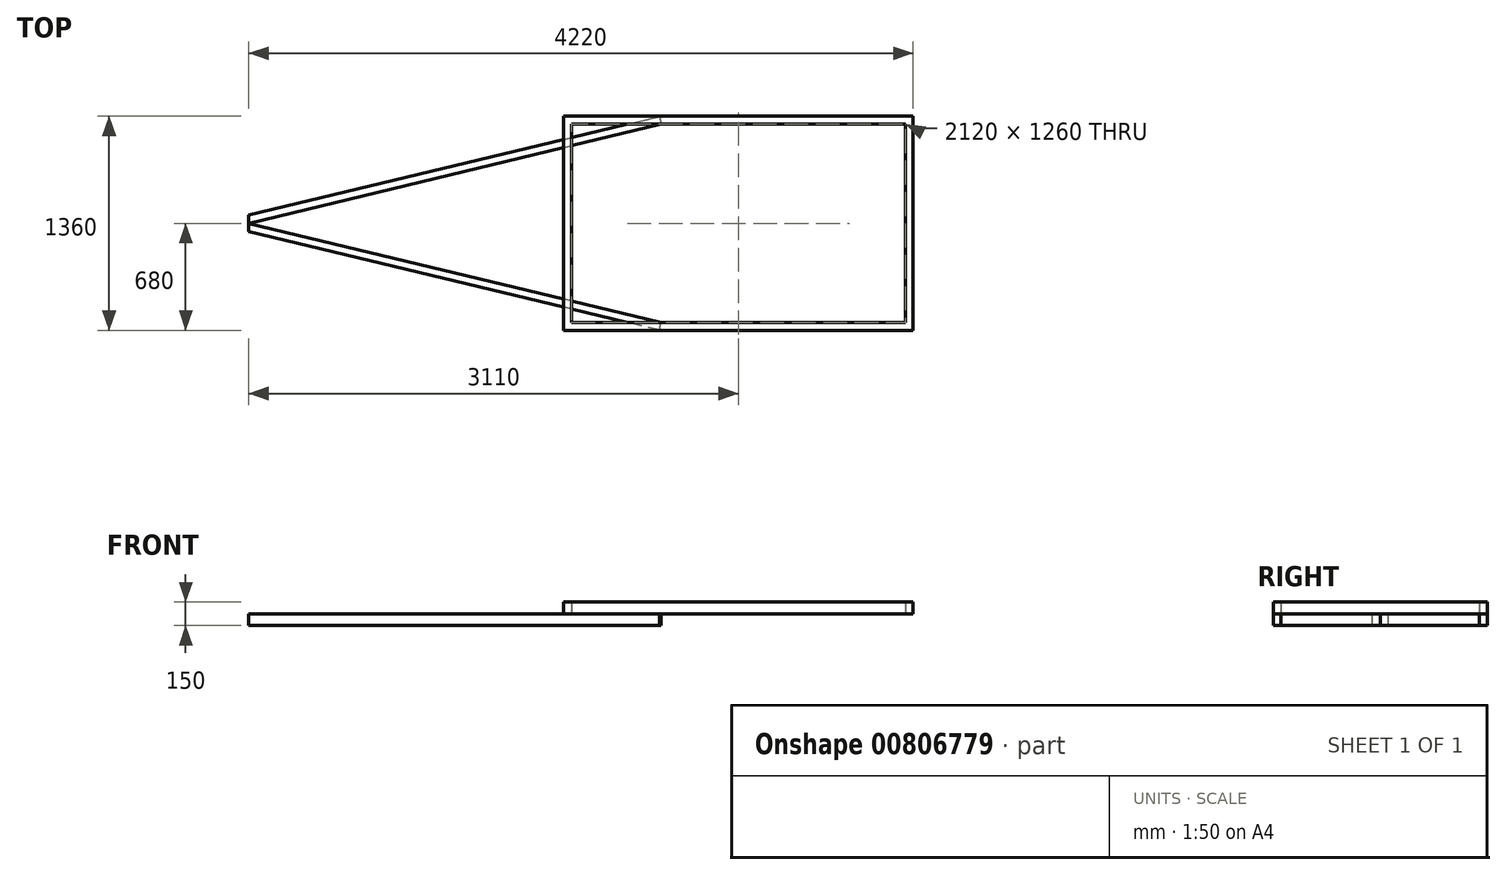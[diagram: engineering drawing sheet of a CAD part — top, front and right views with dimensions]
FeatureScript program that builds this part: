
annotation { "Feature Type Name" : "Feature", "Feature Type Description" : "" }
export const myFeature = defineFeature(function(context is Context, id is Id, definition is map)
    precondition{}
    {
        {
            var Q0;
            Q0=qCreatedBy(makeId("Top.planeOp"),FACE);
            var sketch = newSketch(context, id + "F0", { "sketchPlane" : qUnion([Q0])});
            skLineSegment(sketch, "E0.bottom", {"start": v(1110, 680) * mm, "end": v(-1110, 680) * mm});
            skLineSegment(sketch, "E0.top", {"start": v(1110, -680) * mm, "end": v(-1110, -680) * mm});
            skLineSegment(sketch, "E0.left", {"start": v(1110, 680) * mm, "end": v(1110, -680) * mm});
            skLineSegment(sketch, "E0.right", {"start": v(-1110, 680) * mm, "end": v(-1110, -680) * mm});
            skPoint(sketch, "E0.middle", {"position": v(0, 0) * mm});
            skLineSegment(sketch, "E1.0", {"start": v(1060, 630) * mm, "end": v(-1060, 630) * mm});
            skLineSegment(sketch, "E1.1", {"start": v(1060, 630) * mm, "end": v(1060, -630) * mm});
            skLineSegment(sketch, "E1.2", {"start": v(1060, -630) * mm, "end": v(-1060, -630) * mm});
            skLineSegment(sketch, "E1.3", {"start": v(-1060, 630) * mm, "end": v(-1060, -630) * mm});
            skPoint(sketch, "E2", {"position": v(-490, -630) * mm});
            skPoint(sketch, "E3", {"position": v(-490, 630) * mm});
            skSolve(sketch);
        }
        {
            var Q0;
            Q0=makeQuery(id+"F0.imprint","IMPRINT",FACE,{"disambiguationData":[TD([[makeQuery(id+"F0.imprint","IMPRINT",EDGE,{"derivedFrom":sQuery(id+"F0.wireOp",EDGE,"E0.bottom")}),1.0]])]});
            extrude(context, id + "F1", {"entities" : qUnion([Q0]), "depth" : 75 * mm, "offsetDistance" : 25 * mm});
        }
        {
            var Q0;
            Q0=qCreatedBy(makeId("Top.planeOp"),FACE);
            var sketch = newSketch(context, id + "F2", { "sketchPlane" : qUnion([Q0])});
            skLineSegment(sketch, "E4.0.0", {"start": v(1110, -680) * mm, "end": v(-1110, -680) * mm});
            skLineSegment(sketch, "E4.0.1", {"start": v(-1110, -680) * mm, "end": v(-1110, 680) * mm});
            skLineSegment(sketch, "E4.0.2", {"start": v(-1110, 680) * mm, "end": v(1110, 680) * mm});
            skLineSegment(sketch, "E4.0.3", {"start": v(1110, 680) * mm, "end": v(1110, -680) * mm});
            skLineSegment(sketch, "E5", {"start": v(-3110, -680) * mm, "end": v(-3110, 680) * mm, "construction": true});
            skLineSegment(sketch, "E6", {"start": v(-3110, 0) * mm, "end": v(-1110, 0) * mm, "construction": true});
            skLineSegment(sketch, "E7", {"start": v(-490, -680) * mm, "end": v(-490, 680) * mm, "construction": true});
            skLineSegment(sketch, "E8.0", {"start": v(1060, -630) * mm, "end": v(-1060, -630) * mm});
            skLineSegment(sketch, "E9.0", {"start": v(1060, 630) * mm, "end": v(-1060, 630) * mm});
            skLineSegment(sketch, "E10", {"start": v(-490, -630) * mm, "end": v(-3110, 0) * mm});
            skLineSegment(sketch, "E11", {"start": v(-3110, 0) * mm, "end": v(-490, 630) * mm});
            skLineSegment(sketch, "E12.0", {"start": v(-501.69, -678.61) * mm, "end": v(-3110, -51.43) * mm});
            skLineSegment(sketch, "E13.0", {"start": v(-3110, 51.43) * mm, "end": v(-501.69, 678.61) * mm});
            skLineSegment(sketch, "E14", {"start": v(-3110, -51.43) * mm, "end": v(-3110, 51.43) * mm});
            skLineSegment(sketch, "E15", {"start": v(-501.69, 678.61) * mm, "end": v(-490, 630) * mm});
            skLineSegment(sketch, "E16", {"start": v(-501.69, -678.61) * mm, "end": v(-490, -630) * mm});
            skSolve(sketch);
        }
        {
            var Q0;
            {var subQ0=sQuery(id+"F2.wireOp",EDGE,"E12.0");var subQ1=sQuery(id+"F2.wireOp",EDGE,"E4.0.1");var subQ2=makeQuery(id+"F2.imprint","INTERSECT",VERTEX,{"derivedFrom":[subQ1,subQ0]});Q0=makeQuery(id+"F2.imprint","IMPRINT",FACE,{"disambiguationData":[TD([[makeQuery(id+"F2.imprint","IMPRINT",EDGE,{"disambiguationData":[TD([[subQ2,-1.0]])],"derivedFrom":subQ1}),1.0]])]});}
            var Q1;
            {var subQ0=sQuery(id+"F2.wireOp",EDGE,"E12.0");var subQ1=sQuery(id+"F2.wireOp",EDGE,"E4.0.1");var subQ2=makeQuery(id+"F2.imprint","INTERSECT",VERTEX,{"derivedFrom":[subQ1,subQ0]});Q1=makeQuery(id+"F2.imprint","IMPRINT",FACE,{"disambiguationData":[TD([[makeQuery(id+"F2.imprint","IMPRINT",EDGE,{"disambiguationData":[TD([[subQ2,-1.0]])],"derivedFrom":subQ1}),-1.0]])]});}
            var Q2;
            {var subQ0=sQuery(id+"F2.wireOp",EDGE,"E13.0");var subQ1=sQuery(id+"F2.wireOp",EDGE,"E4.0.1");var subQ2=makeQuery(id+"F2.imprint","INTERSECT",VERTEX,{"derivedFrom":[subQ1,subQ0]});Q2=makeQuery(id+"F2.imprint","IMPRINT",FACE,{"disambiguationData":[TD([[makeQuery(id+"F2.imprint","IMPRINT",EDGE,{"disambiguationData":[TD([[subQ2,1.0]])],"derivedFrom":subQ1}),1.0]])]});}
            var Q3;
            {var subQ0=sQuery(id+"F2.wireOp",EDGE,"E13.0");var subQ1=sQuery(id+"F2.wireOp",EDGE,"E4.0.1");var subQ2=makeQuery(id+"F2.imprint","INTERSECT",VERTEX,{"derivedFrom":[subQ1,subQ0]});Q3=makeQuery(id+"F2.imprint","IMPRINT",FACE,{"disambiguationData":[TD([[makeQuery(id+"F2.imprint","IMPRINT",EDGE,{"disambiguationData":[TD([[subQ2,1.0]])],"derivedFrom":subQ1}),-1.0]])]});}
            var Q4;
            {var subQ0=sQuery(id+"F2.wireOp",EDGE,"E15");Q4=makeQuery(id+"F2.imprint","IMPRINT",FACE,{"disambiguationData":[TD([[makeQuery(id+"F2.imprint","IMPRINT",EDGE,{"derivedFrom":subQ0}),-1.0]])]});}
            var Q5;
            {var subQ0=sQuery(id+"F2.wireOp",EDGE,"E16");Q5=makeQuery(id+"F2.imprint","IMPRINT",FACE,{"disambiguationData":[TD([[makeQuery(id+"F2.imprint","IMPRINT",EDGE,{"derivedFrom":subQ0}),1.0]])]});}
            extrude(context, id + "F3", {"entities" : qUnion([Q0, Q1, Q2, Q3, Q4, Q5]), "oppositeDirection" : true, "depth" : 75 * mm, "offsetDistance" : 25 * mm});
        }
    });
